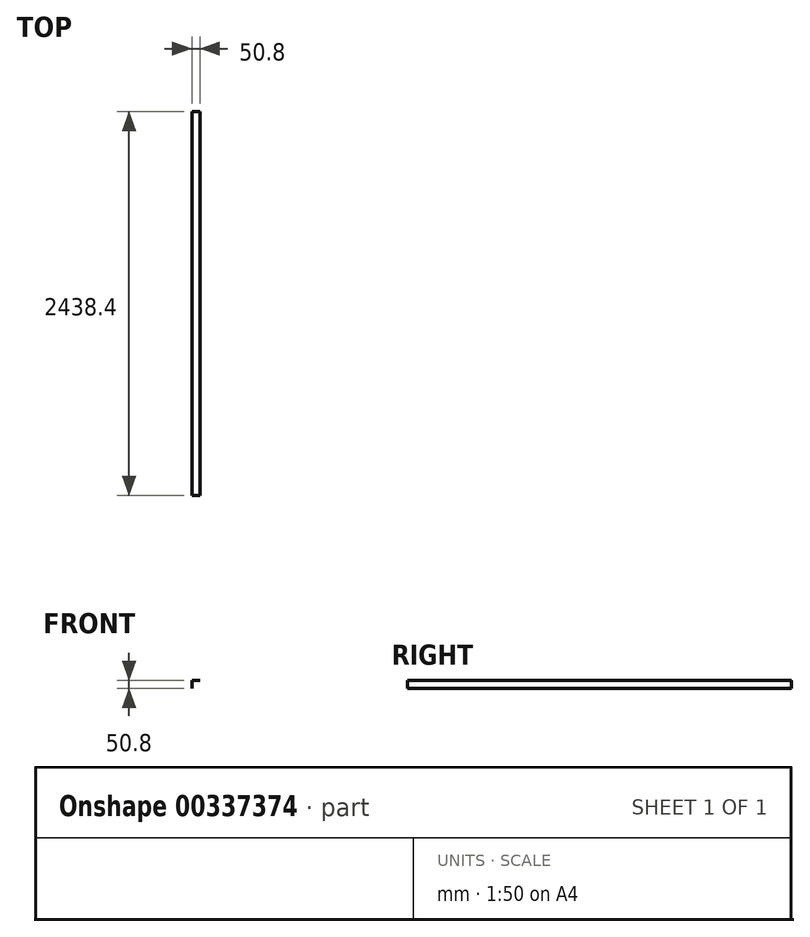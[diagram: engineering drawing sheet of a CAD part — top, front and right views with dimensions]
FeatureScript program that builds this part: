
annotation { "Feature Type Name" : "Feature", "Feature Type Description" : "" }
export const myFeature = defineFeature(function(context is Context, id is Id, definition is map)
    precondition{}
    {
        {
            var Q0;
            Q0=qCreatedBy(makeId("Front.planeOp"),FACE);
            var sketch = newSketch(context, id + "F0", { "sketchPlane" : qUnion([Q0])});
            skLineSegment(sketch, "E0", {"start": v(-70.07, -17.93) * mm, "end": v(-70.07, 32.87) * mm});
            skLineSegment(sketch, "E1", {"start": v(-70.07, 32.87) * mm, "end": v(-19.27, 32.87) * mm});
            skSolve(sketch);
        }
        {
            var Q0;
            Q0 = qSketchRegion(id + "F0", true);
            var Q1;
            Q1=sQuery(id+"F0.wireOp",EDGE,"E1");
            var Q2;
            Q2=sQuery(id+"F0.wireOp",EDGE,"E0");
            extrude(context, id + "F1", {"entities" : qUnion([Q0]), "bodyType" : ToolBodyType.SURFACE, "surfaceEntities" : qUnion([Q1, Q2]), "depth" : 2438.4 * mm});
        }
    });
